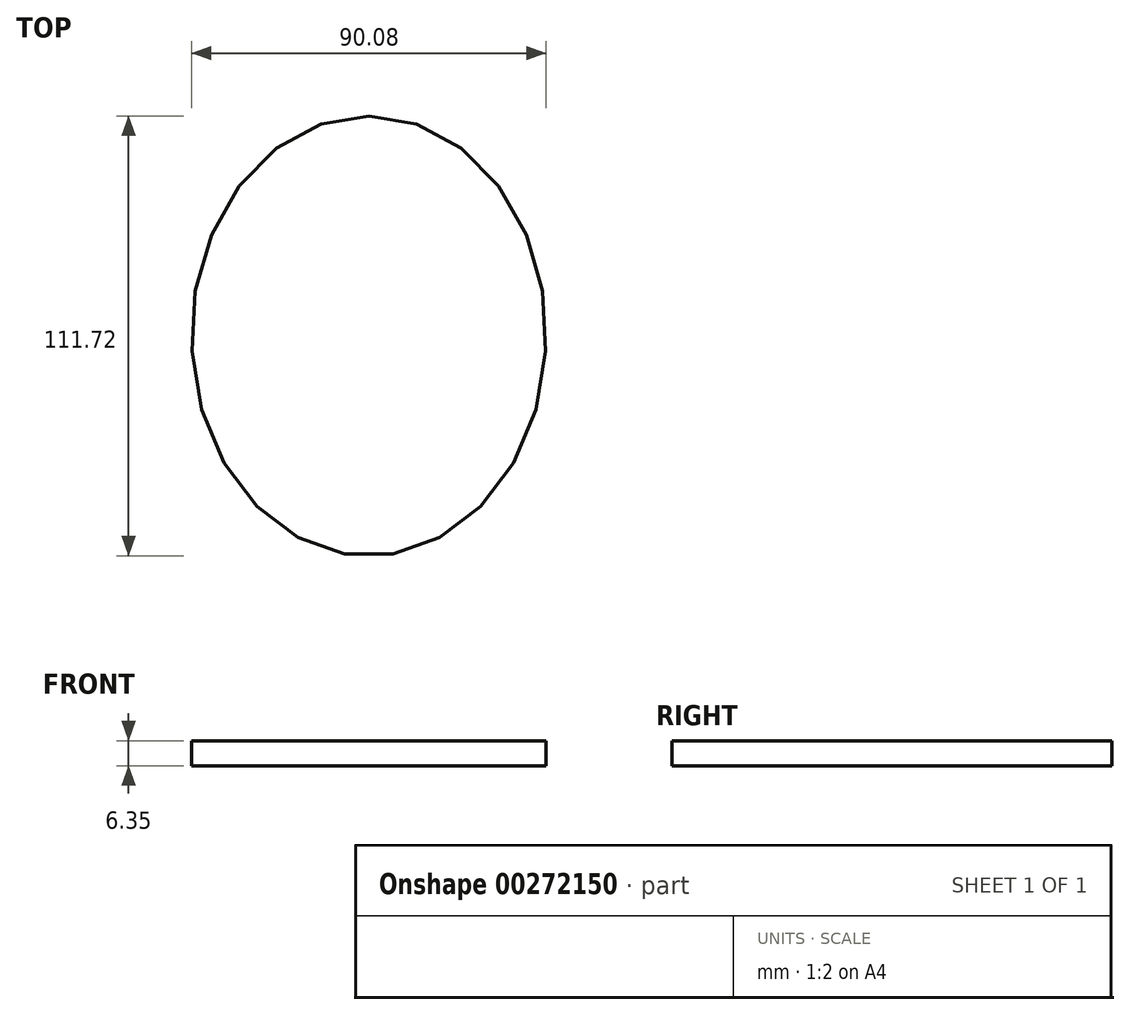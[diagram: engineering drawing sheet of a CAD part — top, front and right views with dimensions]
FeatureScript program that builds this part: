
annotation { "Feature Type Name" : "Feature", "Feature Type Description" : "" }
export const myFeature = defineFeature(function(context is Context, id is Id, definition is map)
    precondition{}
    {
        {
            var Q0;
            Q0=qCreatedBy(makeId("Top.planeOp"),FACE);
            var sketch = newSketch(context, id + "F0", { "sketchPlane" : qUnion([Q0])});
            skEllipse(sketch, "E0", {"center": v(0, 0) * mm, "majorRadius": 55.86 * mm, "minorRadius": 45.04 * mm, "majorAxis": v(0, 1)});
            skSolve(sketch);
        }
        {
            var Q0;
            Q0=makeQuery(id+"F0.imprint","IMPRINT",FACE,{"disambiguationData":[TD([[makeQuery(id+"F0.imprint","IMPRINT",EDGE,{"derivedFrom":sQuery(id+"F0.wireOp",EDGE,"E0")}),1.0]])]});
            extrude(context, id + "F1", {"entities" : qUnion([Q0]), "depth" : 6.35 * mm});
        }
    });
